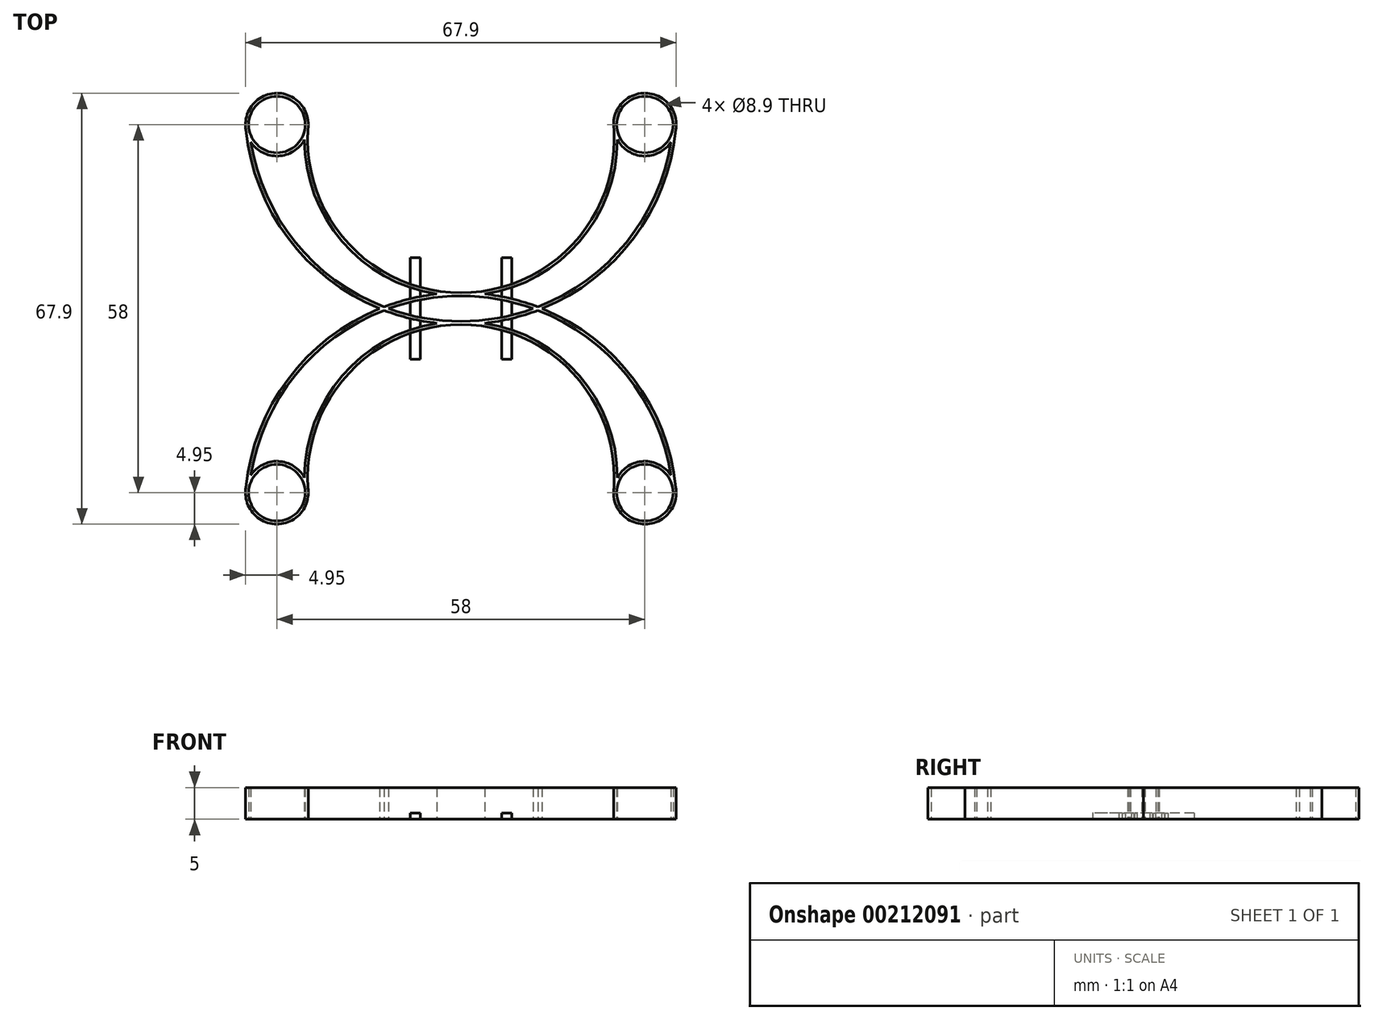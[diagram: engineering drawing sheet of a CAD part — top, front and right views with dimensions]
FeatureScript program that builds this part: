
annotation { "Feature Type Name" : "Feature", "Feature Type Description" : "" }
export const myFeature = defineFeature(function(context is Context, id is Id, definition is map)
    precondition{}
    {
        {
            var Q0;
            Q0=qCreatedBy(makeId("Top.planeOp"),FACE);
            var sketch = newSketch(context, id + "F0", { "sketchPlane" : qUnion([Q0])});
            skCircle(sketch, "E0", {"center": v(-29, 29) * mm, "radius": 4.45 * mm});
            skArc(sketch, "E1.0", {"start": v(-33.13, 26.27) * mm, "mid": v(-28.8, 24.05) * mm, "end": v(-24.66, 26.61) * mm});
            skCircle(sketch, "E2.MirrorC", {"center": v(29, 29) * mm, "radius": 4.45 * mm});
            skArc(sketch, "E3.MirrorC", {"start": v(24.11, 28.2) * mm, "mid": v(29.04, 33.95) * mm, "end": v(33.87, 28.14) * mm});
            skLineSegment(sketch, "E4", {"start": v(0, -2.5) * mm, "end": v(0, 2.5) * mm, "construction": true});
            skPoint(sketch, "E5", {"position": v(-24.05, 29) * mm});
            skPoint(sketch, "E6", {"position": v(24.05, 29) * mm});
            skArc(sketch, "E7", {"start": v(-24.05, 29) * mm, "mid": v(0, 2.5) * mm, "end": v(24.05, 29) * mm});
            skArc(sketch, "E8", {"start": v(-33.95, 29) * mm, "mid": v(0, -2.5) * mm, "end": v(33.95, 29) * mm});
            skPoint(sketch, "E9", {"position": v(-33.95, 29) * mm});
            skPoint(sketch, "E10", {"position": v(33.95, 29) * mm});
            skPoint(sketch, "E11", {"position": v(0, 0) * mm});
            skArc(sketch, "E12.0", {"start": v(-24.55, 29.03) * mm, "mid": v(-24.58, 28.65) * mm, "end": v(-24.61, 28.26) * mm});
            skArc(sketch, "E13.0", {"start": v(-33.45, 29.06) * mm, "mid": v(-33.42, 28.63) * mm, "end": v(-33.38, 28.2) * mm});
            skArc(sketch, "E14.trimOffspring", {"start": v(-33.13, 26.27) * mm, "mid": v(0, -2) * mm, "end": v(33.13, 26.27) * mm});
            skArc(sketch, "E15.trimOffspring", {"start": v(-24.66, 26.61) * mm, "mid": v(0, 2) * mm, "end": v(24.66, 26.61) * mm});
            skArc(sketch, "E16.trimOffspring", {"start": v(-24.11, 28.2) * mm, "mid": v(-29.04, 33.95) * mm, "end": v(-33.87, 28.14) * mm});
            skArc(sketch, "E17.trimOffspring", {"start": v(24.61, 28.26) * mm, "mid": v(24.58, 28.65) * mm, "end": v(24.55, 29.03) * mm});
            skArc(sketch, "E18.trimOffspring", {"start": v(33.38, 28.2) * mm, "mid": v(33.42, 28.63) * mm, "end": v(33.45, 29.06) * mm});
            skArc(sketch, "E19.trimOffspring", {"start": v(33.13, 26.27) * mm, "mid": v(28.8, 24.05) * mm, "end": v(24.66, 26.61) * mm});
            skArc(sketch, "E20.MirrorCS", {"start": v(-24.66, -26.61) * mm, "mid": v(0, -2) * mm, "end": v(24.66, -26.61) * mm});
            skArc(sketch, "E21.MirrorCS", {"start": v(-24.05, -29) * mm, "mid": v(0, -2.5) * mm, "end": v(24.05, -29) * mm});
            skArc(sketch, "E22.MirrorCS", {"start": v(-33.95, -29) * mm, "mid": v(0, 2.5) * mm, "end": v(33.95, -29) * mm});
            skArc(sketch, "E23.MirrorCS", {"start": v(-33.13, -26.27) * mm, "mid": v(0, 2) * mm, "end": v(33.13, -26.27) * mm});
            skArc(sketch, "E24.MirrorCS", {"start": v(-33.13, -26.27) * mm, "mid": v(-28.8, -24.05) * mm, "end": v(-24.66, -26.61) * mm});
            skCircle(sketch, "E25.MirrorC", {"center": v(-29, -29) * mm, "radius": 4.45 * mm});
            skArc(sketch, "E26.MirrorCS", {"start": v(-24.11, -28.2) * mm, "mid": v(-29.04, -33.95) * mm, "end": v(-33.87, -28.14) * mm});
            skArc(sketch, "E27.MirrorCS", {"start": v(33.13, -26.27) * mm, "mid": v(28.8, -24.05) * mm, "end": v(24.66, -26.61) * mm});
            skCircle(sketch, "E28.MirrorC", {"center": v(29, -29) * mm, "radius": 4.45 * mm});
            skArc(sketch, "E29.MirrorCS", {"start": v(24.11, -28.2) * mm, "mid": v(29.04, -33.95) * mm, "end": v(33.87, -28.14) * mm});
            skSolve(sketch);
        }
        {
            var Q0;
            Q0 = qSketchRegion(id + "F0", true);
            var Q1;
            {var subQ0=sQuery(id+"F0.wireOp",EDGE,"E22.MirrorCS");var subQ1=sQuery(id+"F0.wireOp",EDGE,"E14.trimOffspring");var subQ2=makeQuery(id+"F0.imprint","INTERSECT",VERTEX,{"disambiguationData":[OD(0.0)],"derivedFrom":[subQ1,subQ0]});Q1=makeQuery(id+"F0.imprint","IMPRINT",FACE,{"disambiguationData":[TD([[makeQuery(id+"F0.imprint","IMPRINT",EDGE,{"disambiguationData":[TD([[subQ2,-1.0]])],"derivedFrom":subQ1}),1.0]])]});}
            var Q2;
            {var subQ0=sQuery(id+"F0.wireOp",EDGE,"E23.MirrorCS");var subQ1=sQuery(id+"F0.wireOp",EDGE,"E8");var subQ2=makeQuery(id+"F0.imprint","INTERSECT",VERTEX,{"disambiguationData":[OD(0.0)],"derivedFrom":[subQ1,subQ0]});Q2=makeQuery(id+"F0.imprint","IMPRINT",FACE,{"disambiguationData":[TD([[makeQuery(id+"F0.imprint","IMPRINT",EDGE,{"disambiguationData":[TD([[subQ2,-1.0]])],"derivedFrom":subQ1}),1.0]])]});}
            var Q3;
            {var subQ0=sQuery(id+"F0.wireOp",EDGE,"E20.MirrorCS");var subQ1=sQuery(id+"F0.wireOp",EDGE,"E8");var subQ2=makeQuery(id+"F0.imprint","INTERSECT",VERTEX,{"disambiguationData":[OD(1.0)],"derivedFrom":[subQ1,subQ0]});Q3=makeQuery(id+"F0.imprint","IMPRINT",FACE,{"disambiguationData":[TD([[makeQuery(id+"F0.imprint","IMPRINT",EDGE,{"disambiguationData":[TD([[subQ2,-1.0]])],"derivedFrom":subQ1}),1.0]])]});}
            var Q4;
            {var subQ0=sQuery(id+"F0.wireOp",EDGE,"E23.MirrorCS");var subQ1=sQuery(id+"F0.wireOp",EDGE,"E14.trimOffspring");var subQ2=makeQuery(id+"F0.imprint","INTERSECT",VERTEX,{"disambiguationData":[OD(1.0)],"derivedFrom":[subQ1,subQ0]});Q4=makeQuery(id+"F0.imprint","IMPRINT",FACE,{"disambiguationData":[TD([[makeQuery(id+"F0.imprint","IMPRINT",EDGE,{"disambiguationData":[TD([[subQ2,-1.0]])],"derivedFrom":subQ1}),1.0]])]});}
            extrude(context, id + "F1", {"entities" : qUnion([Q0, Q1, Q2, Q3, Q4]), "depth" : 5 * mm});
        }
        {
            var Q0;
            Q0=qCreatedBy(makeId("Top.planeOp"),FACE);
            var sketch = newSketch(context, id + "F2", { "sketchPlane" : qUnion([Q0])});
            skLineSegment(sketch, "E30.bottom", {"start": v(6.4, 8) * mm, "end": v(8, 8) * mm});
            skLineSegment(sketch, "E30.top", {"start": v(6.4, -8) * mm, "end": v(8, -8) * mm});
            skLineSegment(sketch, "E30.left", {"start": v(6.4, 8) * mm, "end": v(6.4, -8) * mm});
            skLineSegment(sketch, "E30.right", {"start": v(8, 8) * mm, "end": v(8, -8) * mm});
            skPoint(sketch, "E31", {"position": v(6.4, 0) * mm});
            skLineSegment(sketch, "E32.MirrorCS", {"start": v(-6.4, 8) * mm, "end": v(-6.4, -8) * mm});
            skLineSegment(sketch, "E33.MirrorCS", {"start": v(-6.4, -8) * mm, "end": v(-8, -8) * mm});
            skLineSegment(sketch, "E34.MirrorCS", {"start": v(-8, 8) * mm, "end": v(-8, -8) * mm});
            skLineSegment(sketch, "E35.MirrorCS", {"start": v(-6.4, 8) * mm, "end": v(-8, 8) * mm});
            skSolve(sketch);
        }
        {
            var Q0;
            Q0 = qSketchRegion(id + "F2", true);
            extrude(context, id + "F3", {"entities" : qUnion([Q0]), "operationType" : NewBodyOperationType.ADD, "depth" : 1 * mm});
        }
    });
